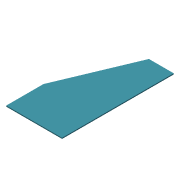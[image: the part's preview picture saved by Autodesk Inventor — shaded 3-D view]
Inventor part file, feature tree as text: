
AUTODESK INVENTOR PART (.ipt)
format: ipt  version: 2014 (Build 180170000, 170)  size: 83,968 bytes
history: native  units: mm
features: extrude x2, sketch x1
ambient origin geometry x8: Origin, YZ Plane, XZ Plane, XY Plane, X Axis, Y Axis, Z Axis, Center Point
bodies: Solid1 (feature_tree)
feature tree (3):
  extrude  "Extrusion1"  Depth=450.0mm
  extrude  "Extrusion2"  Depth=4.0mm TaperAngle=0.0deg
  sketch  "Sketch1"  dims[d0=225.0mm d1=450.0mm d2=4.0mm d3=0.0mm d4=4.0mm d5=0.0mm d8=150.0mm]
